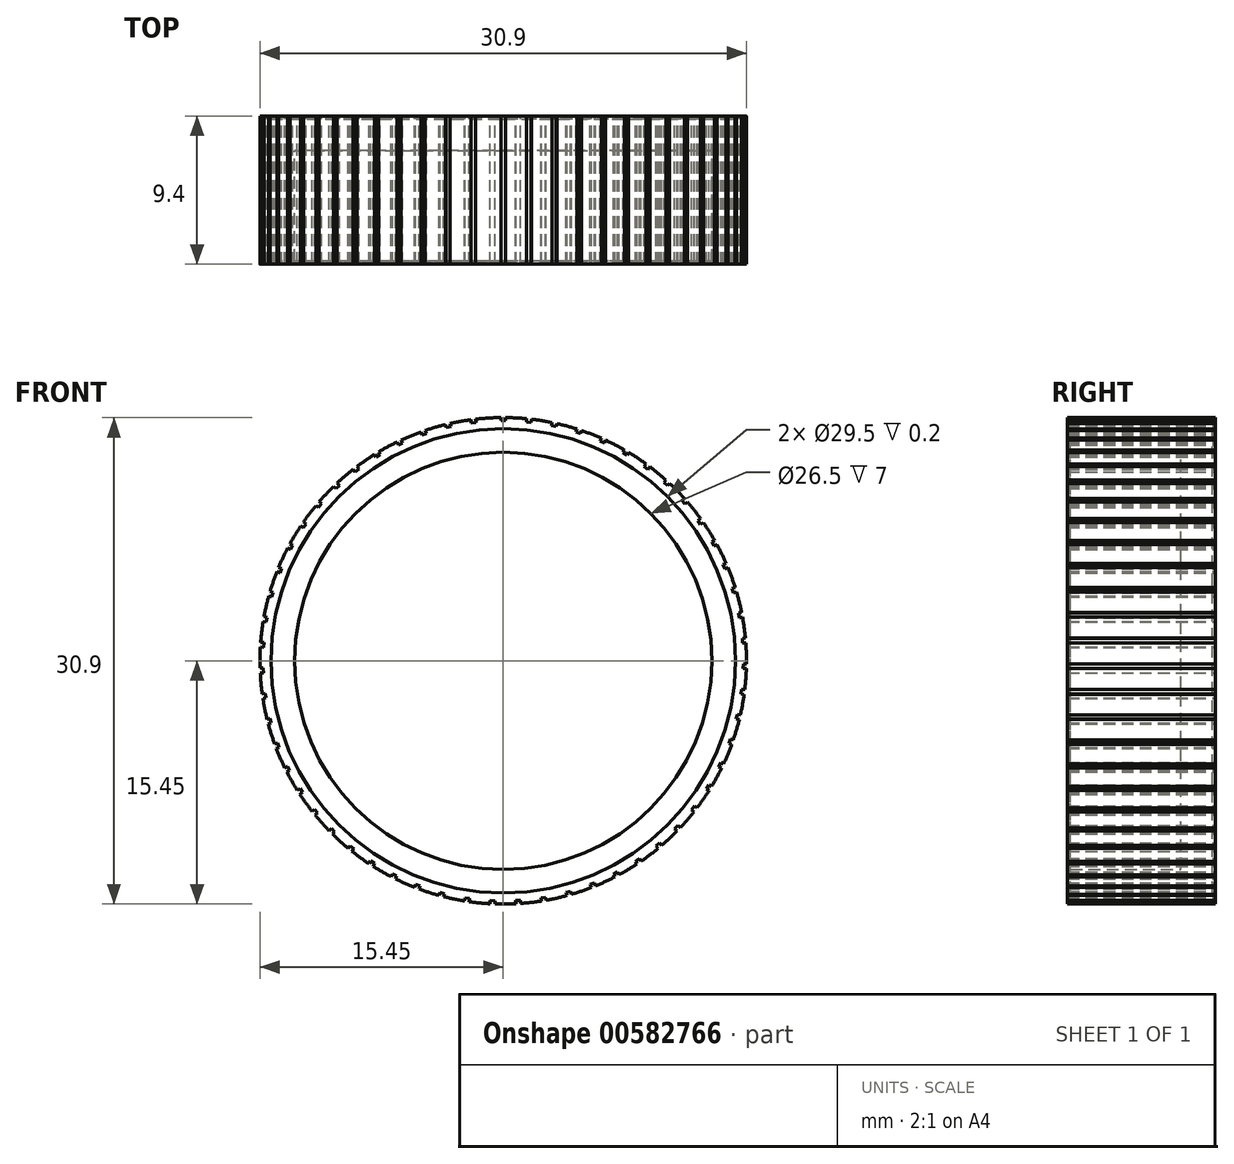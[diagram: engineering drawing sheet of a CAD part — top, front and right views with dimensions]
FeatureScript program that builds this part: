
annotation { "Feature Type Name" : "Feature", "Feature Type Description" : "" }
export const myFeature = defineFeature(function(context is Context, id is Id, definition is map)
    precondition{}
    {
        {
            var Q0;
            Q0=qCreatedBy(makeId("Front.planeOp"),FACE);
            var sketch = newSketch(context, id + "F0", { "sketchPlane" : qUnion([Q0])});
            skCircle(sketch, "E0", {"center": v(0, 0) * mm, "radius": 14.75 * mm});
            skCircle(sketch, "E1.0", {"center": v(0, 0) * mm, "radius": 13.25 * mm});
            skSolve(sketch);
        }
        {
            var Q0;
            Q0=makeQuery(id+"F0.imprint","IMPRINT",FACE,{"disambiguationData":[TD([[makeQuery(id+"F0.imprint","IMPRINT",EDGE,{"derivedFrom":sQuery(id+"F0.wireOp",EDGE,"E0")}),1.0]])]});
            extrude(context, id + "F1", {"entities" : qUnion([Q0]), "depth" : 9 * mm});
        }
        {
            var Q0;
            Q0=qCreatedBy(makeId("Front.planeOp"),FACE);
            var sketch = newSketch(context, id + "F2", { "sketchPlane" : qUnion([Q0])});
            skCircle(sketch, "E2", {"center": v(0, 0) * mm, "radius": 13.25 * mm});
            skSolve(sketch);
        }
        {
            var Q0;
            {var subQ0=sQuery(id+"F2.wireOp",EDGE,"3keaKyCw-Lqcn-IX1E-cnb6-a4ZA5nUTnozF");Q0=makeQuery(id+"F2.imprint","IMPRINT",FACE,{"disambiguationData":[TD([[makeQuery(id+"F2.imprint","IMPRINT",EDGE,{"derivedFrom":subQ0}),1.0]])]});}
            var Q1;
            {var subQ0=sQuery(id+"F2.wireOp",EDGE,"mG6a82be-69iQ-I6sY-IQmd-3RMDi1MG6bG6");Q1=makeQuery(id+"F2.imprint","IMPRINT",FACE,{"disambiguationData":[TD([[makeQuery(id+"F2.imprint","IMPRINT",EDGE,{"derivedFrom":subQ0}),1.0]])]});}
            var Q2;
            {var subQ0=sQuery(id+"F2.wireOp",EDGE,"hU7no7Vv-n9lv-C5YX-Tx9H-Se0t01cKzEbt");Q2=makeQuery(id+"F2.imprint","IMPRINT",FACE,{"disambiguationData":[TD([[makeQuery(id+"F2.imprint","IMPRINT",EDGE,{"derivedFrom":subQ0}),-1.0]])]});}
            var Q3;
            {var subQ0=sQuery(id+"F2.wireOp",EDGE,"w8KxwOBV-seBn-yTGC-fRHL-n6Ncswi49O3E");Q3=makeQuery(id+"F2.imprint","IMPRINT",FACE,{"disambiguationData":[TD([[makeQuery(id+"F2.imprint","IMPRINT",EDGE,{"derivedFrom":subQ0}),1.0]])]});}
            var Q4;
            {var subQ0=sQuery(id+"F2.wireOp",EDGE,"HlxNPSqv-OCNp-PsbN-OUw0-2Dy4POzx889V");Q4=makeQuery(id+"F2.imprint","IMPRINT",FACE,{"disambiguationData":[TD([[makeQuery(id+"F2.imprint","IMPRINT",EDGE,{"derivedFrom":subQ0}),-1.0]])]});}
            var Q5;
            {var subQ0=sQuery(id+"F2.wireOp",EDGE,"GymvrA6v-V9iu-6h20-Pxzl-EcmsKYmL8GNP");Q5=makeQuery(id+"F2.imprint","IMPRINT",FACE,{"disambiguationData":[TD([[makeQuery(id+"F2.imprint","IMPRINT",EDGE,{"derivedFrom":subQ0}),-1.0]])]});}
            var Q6;
            {var subQ0=sQuery(id+"F2.wireOp",EDGE,"8rj0P59o-sSCo-hf25-OtZS-1FKQbejQrVaP");Q6=makeQuery(id+"F2.imprint","IMPRINT",FACE,{"disambiguationData":[TD([[makeQuery(id+"F2.imprint","IMPRINT",EDGE,{"derivedFrom":subQ0}),-1.0]])]});}
            var Q7;
            {var subQ0=sQuery(id+"F2.wireOp",EDGE,"0XGIMpHW-GgJE-la3a-LZoR-t8cl6haSuso4");Q7=makeQuery(id+"F2.imprint","IMPRINT",FACE,{"disambiguationData":[TD([[makeQuery(id+"F2.imprint","IMPRINT",EDGE,{"derivedFrom":subQ0}),-1.0]])]});}
            var Q8;
            {var subQ1=sQuery(id+"F2.wireOp",EDGE,"cdTxKz4M-8jyy-kseZ-T7IN-5LjAP2MmduU8");var subQ11=sQuery(id+"F2.wireOp",EDGE,"QO7leQhL-Iaco-JcvS-EdGk-ymootaYFfpQf");var subQ12=makeQuery(id+"F2.imprint","INTERSECT",VERTEX,{"derivedFrom":[subQ1,subQ11]});Q8=makeQuery(id+"F2.imprint","IMPRINT",FACE,{"disambiguationData":[TD([[makeQuery(id+"F2.imprint","IMPRINT",EDGE,{"disambiguationData":[TD([[subQ12,-1.0]])],"derivedFrom":subQ1}),-1.0]])]});}
            var Q9;
            {var subQ9=sQuery(id+"F2.wireOp",EDGE,"aPjoHP4x-gmIf-1ttG-AxL6-nKyPkYbaChfL");var subQ11=sQuery(id+"F2.wireOp",EDGE,"8Gy7XW5u-FLYC-EZkC-LaJu-Y9E0anSlFcaX");var subQ12=makeQuery(id+"F2.imprint","INTERSECT",VERTEX,{"derivedFrom":[subQ9,subQ11]});Q9=makeQuery(id+"F2.imprint","IMPRINT",FACE,{"disambiguationData":[TD([[makeQuery(id+"F2.imprint","IMPRINT",EDGE,{"disambiguationData":[TD([[subQ12,-1.0]])],"derivedFrom":subQ9}),1.0]])]});}
            var Q10;
            {var subQ3=sQuery(id+"F2.wireOp",EDGE,"oQIrEx9H-TGKM-4inS-EEnm-a9sFU0Elgldt");var subQ10=sQuery(id+"F2.wireOp",EDGE,"GY7wzPKg-8jDN-OJM1-rmuM-SVpCFXL6a0nh");var subQ11=makeQuery(id+"F2.imprint","INTERSECT",VERTEX,{"derivedFrom":[subQ3,subQ10]});Q10=makeQuery(id+"F2.imprint","IMPRINT",FACE,{"disambiguationData":[TD([[makeQuery(id+"F2.imprint","IMPRINT",EDGE,{"disambiguationData":[TD([[subQ11,-1.0]])],"derivedFrom":subQ3}),1.0]])]});}
            var Q11;
            {var subQ7=sQuery(id+"F2.wireOp",EDGE,"PrWXmb39-ACQH-pRjp-kugf-BFPo7j13sEjC");var subQ9=sQuery(id+"F2.wireOp",EDGE,"5D8PRt4u-vBLA-oPdB-r0au-RqC48Tny4yqn");var subQ10=makeQuery(id+"F2.imprint","INTERSECT",VERTEX,{"derivedFrom":[subQ7,subQ9]});Q11=makeQuery(id+"F2.imprint","IMPRINT",FACE,{"disambiguationData":[TD([[makeQuery(id+"F2.imprint","IMPRINT",EDGE,{"disambiguationData":[TD([[subQ10,1.0]])],"derivedFrom":subQ7}),1.0]])]});}
            var Q12;
            {var subQ5=sQuery(id+"F2.wireOp",EDGE,"PrWXmb39-ACQH-pRjp-kugf-BFPo7j13sEjC");var subQ7=sQuery(id+"F2.wireOp",EDGE,"GY7wzPKg-8jDN-OJM1-rmuM-SVpCFXL6a0nh");var subQ12=makeQuery(id+"F2.imprint","INTERSECT",VERTEX,{"derivedFrom":[subQ5,subQ7]});Q12=makeQuery(id+"F2.imprint","IMPRINT",FACE,{"disambiguationData":[TD([[makeQuery(id+"F2.imprint","IMPRINT",EDGE,{"disambiguationData":[TD([[subQ12,-1.0]])],"derivedFrom":subQ5}),-1.0]])]});}
            var Q13;
            {var subQ0=sQuery(id+"F2.wireOp",EDGE,"5D8PRt4u-vBLA-oPdB-r0au-RqC48Tny4yqn");var subQ1=sQuery(id+"F2.wireOp",EDGE,"mz7uVP0I-VIxG-UEDP-77Vf-fuGD4AyohhOF");var subQ2=makeQuery(id+"F2.imprint","INTERSECT",VERTEX,{"derivedFrom":[subQ1,subQ0]});Q13=makeQuery(id+"F2.imprint","IMPRINT",FACE,{"disambiguationData":[TD([[makeQuery(id+"F2.imprint","IMPRINT",EDGE,{"disambiguationData":[TD([[subQ2,1.0]])],"derivedFrom":subQ1}),-1.0]])]});}
            var Q14;
            {var subQ0=sQuery(id+"F2.wireOp",EDGE,"GY7wzPKg-8jDN-OJM1-rmuM-SVpCFXL6a0nh");var subQ8=sQuery(id+"F2.wireOp",EDGE,"eVlDfYWF-ZmK0-dg2n-POrD-hiu8iOGEyNgQ");var subQ14=makeQuery(id+"F2.imprint","INTERSECT",VERTEX,{"derivedFrom":[subQ8,subQ0]});Q14=makeQuery(id+"F2.imprint","IMPRINT",FACE,{"disambiguationData":[TD([[makeQuery(id+"F2.imprint","IMPRINT",EDGE,{"disambiguationData":[TD([[subQ14,1.0]])],"derivedFrom":subQ8}),1.0]])]});}
            var Q15;
            {var subQ0=sQuery(id+"F2.wireOp",EDGE,"8Gy7XW5u-FLYC-EZkC-LaJu-Y9E0anSlFcaX");var subQ1=sQuery(id+"F2.wireOp",EDGE,"pedmM5iB-94l6-CeBW-8z7l-qVik7crMEmoY");var subQ2=makeQuery(id+"F2.imprint","INTERSECT",VERTEX,{"derivedFrom":[subQ1,subQ0]});Q15=makeQuery(id+"F2.imprint","IMPRINT",FACE,{"disambiguationData":[TD([[makeQuery(id+"F2.imprint","IMPRINT",EDGE,{"disambiguationData":[TD([[subQ2,-1.0]])],"derivedFrom":subQ1}),-1.0]])]});}
            var Q16;
            {var subQ3=sQuery(id+"F2.wireOp",EDGE,"aPjoHP4x-gmIf-1ttG-AxL6-nKyPkYbaChfL");var subQ5=sQuery(id+"F2.wireOp",EDGE,"GY7wzPKg-8jDN-OJM1-rmuM-SVpCFXL6a0nh");var subQ10=makeQuery(id+"F2.imprint","INTERSECT",VERTEX,{"derivedFrom":[subQ3,subQ5]});Q16=makeQuery(id+"F2.imprint","IMPRINT",FACE,{"disambiguationData":[TD([[makeQuery(id+"F2.imprint","IMPRINT",EDGE,{"disambiguationData":[TD([[subQ10,1.0]])],"derivedFrom":subQ3}),-1.0]])]});}
            var Q17;
            {var subQ0=sQuery(id+"F2.wireOp",EDGE,"GY7wzPKg-8jDN-OJM1-rmuM-SVpCFXL6a0nh");var subQ1=sQuery(id+"F2.wireOp",EDGE,"eVlDfYWF-ZmK0-dg2n-POrD-hiu8iOGEyNgQ");var subQ2=makeQuery(id+"F2.imprint","INTERSECT",VERTEX,{"derivedFrom":[subQ1,subQ0]});Q17=makeQuery(id+"F2.imprint","IMPRINT",FACE,{"disambiguationData":[TD([[makeQuery(id+"F2.imprint","IMPRINT",EDGE,{"disambiguationData":[TD([[subQ2,1.0]])],"derivedFrom":subQ1}),-1.0]])]});}
            var Q18;
            {var subQ0=sQuery(id+"F2.wireOp",EDGE,"GY7wzPKg-8jDN-OJM1-rmuM-SVpCFXL6a0nh");var subQ1=sQuery(id+"F2.wireOp",EDGE,"nDKB6Nuh-on1I-7DlA-8arG-BoZKlbM7OEjq");var subQ2=makeQuery(id+"F2.imprint","INTERSECT",VERTEX,{"derivedFrom":[subQ1,subQ0]});Q18=makeQuery(id+"F2.imprint","IMPRINT",FACE,{"disambiguationData":[TD([[makeQuery(id+"F2.imprint","IMPRINT",EDGE,{"disambiguationData":[TD([[subQ2,1.0]])],"derivedFrom":subQ1}),1.0]])]});}
            var Q19;
            {var subQ0=sQuery(id+"F2.wireOp",EDGE,"GY7wzPKg-8jDN-OJM1-rmuM-SVpCFXL6a0nh");var subQ1=sQuery(id+"F2.wireOp",EDGE,"pedmM5iB-94l6-CeBW-8z7l-qVik7crMEmoY");var subQ2=makeQuery(id+"F2.imprint","INTERSECT",VERTEX,{"derivedFrom":[subQ1,subQ0]});Q19=makeQuery(id+"F2.imprint","IMPRINT",FACE,{"disambiguationData":[TD([[makeQuery(id+"F2.imprint","IMPRINT",EDGE,{"disambiguationData":[TD([[subQ2,1.0]])],"derivedFrom":subQ1}),-1.0]])]});}
            var Q20;
            {var subQ0=sQuery(id+"F2.wireOp",EDGE,"GY7wzPKg-8jDN-OJM1-rmuM-SVpCFXL6a0nh");var subQ1=sQuery(id+"F2.wireOp",EDGE,"aPjoHP4x-gmIf-1ttG-AxL6-nKyPkYbaChfL");var subQ2=makeQuery(id+"F2.imprint","INTERSECT",VERTEX,{"derivedFrom":[subQ1,subQ0]});Q20=makeQuery(id+"F2.imprint","IMPRINT",FACE,{"disambiguationData":[TD([[makeQuery(id+"F2.imprint","IMPRINT",EDGE,{"disambiguationData":[TD([[subQ2,1.0]])],"derivedFrom":subQ1}),1.0]])]});}
            var Q21;
            {var subQ0=sQuery(id+"F2.wireOp",EDGE,"GY7wzPKg-8jDN-OJM1-rmuM-SVpCFXL6a0nh");var subQ1=sQuery(id+"F2.wireOp",EDGE,"ySy2fclQ-QHqK-LRJv-mab4-BJFxhKYbme3X");var subQ2=makeQuery(id+"F2.imprint","INTERSECT",VERTEX,{"derivedFrom":[subQ1,subQ0]});Q21=makeQuery(id+"F2.imprint","IMPRINT",FACE,{"disambiguationData":[TD([[makeQuery(id+"F2.imprint","IMPRINT",EDGE,{"disambiguationData":[TD([[subQ2,-1.0]])],"derivedFrom":subQ1}),1.0]])]});}
            var Q22;
            {var subQ0=sQuery(id+"F2.wireOp",EDGE,"GY7wzPKg-8jDN-OJM1-rmuM-SVpCFXL6a0nh");var subQ1=sQuery(id+"F2.wireOp",EDGE,"oQIrEx9H-TGKM-4inS-EEnm-a9sFU0Elgldt");var subQ2=makeQuery(id+"F2.imprint","INTERSECT",VERTEX,{"derivedFrom":[subQ1,subQ0]});Q22=makeQuery(id+"F2.imprint","IMPRINT",FACE,{"disambiguationData":[TD([[makeQuery(id+"F2.imprint","IMPRINT",EDGE,{"disambiguationData":[TD([[subQ2,-1.0]])],"derivedFrom":subQ1}),-1.0]])]});}
            var Q23;
            {var subQ0=sQuery(id+"F2.wireOp",EDGE,"GY7wzPKg-8jDN-OJM1-rmuM-SVpCFXL6a0nh");var subQ1=sQuery(id+"F2.wireOp",EDGE,"PrWXmb39-ACQH-pRjp-kugf-BFPo7j13sEjC");var subQ2=makeQuery(id+"F2.imprint","INTERSECT",VERTEX,{"derivedFrom":[subQ1,subQ0]});Q23=makeQuery(id+"F2.imprint","IMPRINT",FACE,{"disambiguationData":[TD([[makeQuery(id+"F2.imprint","IMPRINT",EDGE,{"disambiguationData":[TD([[subQ2,-1.0]])],"derivedFrom":subQ1}),1.0]])]});}
            var Q24;
            {var subQ0=sQuery(id+"F2.wireOp",EDGE,"GY7wzPKg-8jDN-OJM1-rmuM-SVpCFXL6a0nh");var subQ1=sQuery(id+"F2.wireOp",EDGE,"mz7uVP0I-VIxG-UEDP-77Vf-fuGD4AyohhOF");var subQ2=makeQuery(id+"F2.imprint","INTERSECT",VERTEX,{"derivedFrom":[subQ1,subQ0]});Q24=makeQuery(id+"F2.imprint","IMPRINT",FACE,{"disambiguationData":[TD([[makeQuery(id+"F2.imprint","IMPRINT",EDGE,{"disambiguationData":[TD([[subQ2,-1.0]])],"derivedFrom":subQ1}),-1.0]])]});}
            var Q25;
            Q25=makeQuery(id+"F2.imprint","IMPRINT",FACE,{"disambiguationData":[TD([[makeQuery(id+"F2.imprint","IMPRINT",EDGE,{"derivedFrom":sQuery(id+"F2.wireOp",EDGE,"E2")}),1.0]])]});
            extrude(context, id + "F3", {"entities" : qUnion([Q0, Q1, Q2, Q3, Q4, Q5, Q6, Q7, Q8, Q9, Q10, Q11, Q12, Q13, Q14, Q15, Q16, Q17, Q18, Q19, Q20, Q21, Q22, Q23, Q24, Q25]), "operationType" : NewBodyOperationType.ADD, "depth" : 2 * mm});
        }
        {
            var Q0;
            Q0=qCreatedBy(makeId("Front.planeOp"),FACE);
            var sketch = newSketch(context, id + "F4", { "sketchPlane" : qUnion([Q0])});
            skCircle(sketch, "E3", {"center": v(0, 0) * mm, "radius": 15.45 * mm});
            skCircle(sketch, "E4", {"center": v(0, 0) * mm, "radius": 14.75 * mm});
            skLineSegment(sketch, "E5.bottom", {"start": v(0.15, 15.45) * mm, "end": v(-0.15, 15.45) * mm});
            skLineSegment(sketch, "E5.top", {"start": v(0.15, 15.25) * mm, "end": v(-0.15, 15.25) * mm});
            skLineSegment(sketch, "E5.left", {"start": v(0.15, 15.45) * mm, "end": v(0.15, 15.25) * mm});
            skLineSegment(sketch, "E5.right", {"start": v(-0.15, 15.45) * mm, "end": v(-0.15, 15.25) * mm});
            skLineSegment(sketch, "E6.1.0", {"start": v(1.49, 15.38) * mm, "end": v(1.47, 15.18) * mm});
            skLineSegment(sketch, "E6.1.1", {"start": v(1.79, 15.35) * mm, "end": v(1.77, 15.15) * mm});
            skLineSegment(sketch, "E6.1.2", {"start": v(1.77, 15.15) * mm, "end": v(1.47, 15.18) * mm});
            skLineSegment(sketch, "E6.1.3", {"start": v(1.79, 15.35) * mm, "end": v(1.49, 15.38) * mm});
            skLineSegment(sketch, "E6.2.0", {"start": v(3.11, 15.13) * mm, "end": v(3.07, 14.94) * mm});
            skLineSegment(sketch, "E6.2.1", {"start": v(3.4, 15.07) * mm, "end": v(3.36, 14.87) * mm});
            skLineSegment(sketch, "E6.2.2", {"start": v(3.36, 14.87) * mm, "end": v(3.07, 14.94) * mm});
            skLineSegment(sketch, "E6.2.3", {"start": v(3.4, 15.07) * mm, "end": v(3.11, 15.13) * mm});
            skLineSegment(sketch, "E6.3.0", {"start": v(4.7, 14.72) * mm, "end": v(4.63, 14.53) * mm});
            skLineSegment(sketch, "E6.3.1", {"start": v(4.98, 14.62) * mm, "end": v(4.92, 14.43) * mm});
            skLineSegment(sketch, "E6.3.2", {"start": v(4.92, 14.43) * mm, "end": v(4.63, 14.53) * mm});
            skLineSegment(sketch, "E6.3.3", {"start": v(4.98, 14.62) * mm, "end": v(4.7, 14.72) * mm});
            skLineSegment(sketch, "E6.4.0", {"start": v(6.23, 14.14) * mm, "end": v(6.15, 13.96) * mm});
            skLineSegment(sketch, "E6.4.1", {"start": v(6.5, 14.01) * mm, "end": v(6.42, 13.83) * mm});
            skLineSegment(sketch, "E6.4.2", {"start": v(6.42, 13.83) * mm, "end": v(6.15, 13.96) * mm});
            skLineSegment(sketch, "E6.4.3", {"start": v(6.5, 14.01) * mm, "end": v(6.23, 14.14) * mm});
            skLineSegment(sketch, "E6.5.0", {"start": v(7.7, 13.4) * mm, "end": v(7.6, 13.23) * mm});
            skLineSegment(sketch, "E6.5.1", {"start": v(7.95, 13.25) * mm, "end": v(7.85, 13.07) * mm});
            skLineSegment(sketch, "E6.5.2", {"start": v(7.85, 13.07) * mm, "end": v(7.6, 13.23) * mm});
            skLineSegment(sketch, "E6.5.3", {"start": v(7.95, 13.25) * mm, "end": v(7.7, 13.4) * mm});
            skLineSegment(sketch, "E6.6.0", {"start": v(9.07, 12.5) * mm, "end": v(8.95, 12.35) * mm});
            skLineSegment(sketch, "E6.6.1", {"start": v(9.31, 12.33) * mm, "end": v(9.2, 12.17) * mm});
            skLineSegment(sketch, "E6.6.2", {"start": v(9.2, 12.17) * mm, "end": v(8.95, 12.35) * mm});
            skLineSegment(sketch, "E6.6.3", {"start": v(9.31, 12.33) * mm, "end": v(9.07, 12.5) * mm});
            skLineSegment(sketch, "E6.7.0", {"start": v(10.35, 11.47) * mm, "end": v(10.21, 11.33) * mm});
            skLineSegment(sketch, "E6.7.1", {"start": v(10.57, 11.27) * mm, "end": v(10.43, 11.12) * mm});
            skLineSegment(sketch, "E6.7.2", {"start": v(10.43, 11.12) * mm, "end": v(10.21, 11.33) * mm});
            skLineSegment(sketch, "E6.7.3", {"start": v(10.57, 11.27) * mm, "end": v(10.35, 11.47) * mm});
            skLineSegment(sketch, "E6.8.0", {"start": v(11.5, 10.31) * mm, "end": v(11.35, 10.18) * mm});
            skLineSegment(sketch, "E6.8.1", {"start": v(11.7, 10.09) * mm, "end": v(11.55, 9.96) * mm});
            skLineSegment(sketch, "E6.8.2", {"start": v(11.55, 9.96) * mm, "end": v(11.35, 10.18) * mm});
            skLineSegment(sketch, "E6.8.3", {"start": v(11.7, 10.09) * mm, "end": v(11.5, 10.31) * mm});
            skLineSegment(sketch, "E6.9.0", {"start": v(12.53, 9.04) * mm, "end": v(12.37, 8.92) * mm});
            skLineSegment(sketch, "E6.9.1", {"start": v(12.7, 8.8) * mm, "end": v(12.54, 8.68) * mm});
            skLineSegment(sketch, "E6.9.2", {"start": v(12.54, 8.68) * mm, "end": v(12.37, 8.92) * mm});
            skLineSegment(sketch, "E6.9.3", {"start": v(12.7, 8.8) * mm, "end": v(12.53, 9.04) * mm});
            skLineSegment(sketch, "E6.10.0", {"start": v(13.42, 7.66) * mm, "end": v(13.24, 7.56) * mm});
            skLineSegment(sketch, "E6.10.1", {"start": v(13.57, 7.4) * mm, "end": v(13.4, 7.3) * mm});
            skLineSegment(sketch, "E6.10.2", {"start": v(13.4, 7.3) * mm, "end": v(13.24, 7.56) * mm});
            skLineSegment(sketch, "E6.10.3", {"start": v(13.57, 7.4) * mm, "end": v(13.42, 7.66) * mm});
            skLineSegment(sketch, "E6.11.0", {"start": v(14.16, 6.2) * mm, "end": v(13.97, 6.11) * mm});
            skLineSegment(sketch, "E6.11.1", {"start": v(14.27, 5.92) * mm, "end": v(14.09, 5.84) * mm});
            skLineSegment(sketch, "E6.11.2", {"start": v(14.09, 5.84) * mm, "end": v(13.97, 6.11) * mm});
            skLineSegment(sketch, "E6.11.3", {"start": v(14.27, 5.92) * mm, "end": v(14.16, 6.2) * mm});
            skLineSegment(sketch, "E6.12.0", {"start": v(14.73, 4.66) * mm, "end": v(14.54, 4.6) * mm});
            skLineSegment(sketch, "E6.12.1", {"start": v(14.82, 4.37) * mm, "end": v(14.63, 4.31) * mm});
            skLineSegment(sketch, "E6.12.2", {"start": v(14.63, 4.31) * mm, "end": v(14.54, 4.6) * mm});
            skLineSegment(sketch, "E6.12.3", {"start": v(14.82, 4.37) * mm, "end": v(14.73, 4.66) * mm});
            skLineSegment(sketch, "E6.13.0", {"start": v(15.14, 3.07) * mm, "end": v(14.95, 3.03) * mm});
            skLineSegment(sketch, "E6.13.1", {"start": v(15.2, 2.77) * mm, "end": v(15, 2.74) * mm});
            skLineSegment(sketch, "E6.13.2", {"start": v(15, 2.74) * mm, "end": v(14.95, 3.03) * mm});
            skLineSegment(sketch, "E6.13.3", {"start": v(15.2, 2.77) * mm, "end": v(15.14, 3.07) * mm});
            skLineSegment(sketch, "E6.14.0", {"start": v(15.38, 1.45) * mm, "end": v(15.18, 1.43) * mm});
            skLineSegment(sketch, "E6.14.1", {"start": v(15.4, 1.15) * mm, "end": v(15.2, 1.13) * mm});
            skLineSegment(sketch, "E6.14.2", {"start": v(15.2, 1.13) * mm, "end": v(15.18, 1.43) * mm});
            skLineSegment(sketch, "E6.14.3", {"start": v(15.4, 1.15) * mm, "end": v(15.38, 1.45) * mm});
            skLineSegment(sketch, "E6.15.0", {"start": v(15.45, -0.2) * mm, "end": v(15.25, -0.19) * mm});
            skLineSegment(sketch, "E6.15.1", {"start": v(15.44, -0.5) * mm, "end": v(15.24, -0.49) * mm});
            skLineSegment(sketch, "E6.15.2", {"start": v(15.24, -0.49) * mm, "end": v(15.25, -0.19) * mm});
            skLineSegment(sketch, "E6.15.3", {"start": v(15.44, -0.5) * mm, "end": v(15.45, -0.2) * mm});
            skLineSegment(sketch, "E6.16.0", {"start": v(15.34, -1.83) * mm, "end": v(15.14, -1.8) * mm});
            skLineSegment(sketch, "E6.16.1", {"start": v(15.3, -2.13) * mm, "end": v(15.1, -2.1) * mm});
            skLineSegment(sketch, "E6.16.2", {"start": v(15.1, -2.1) * mm, "end": v(15.14, -1.8) * mm});
            skLineSegment(sketch, "E6.16.3", {"start": v(15.3, -2.13) * mm, "end": v(15.34, -1.83) * mm});
            skLineSegment(sketch, "E6.17.0", {"start": v(15.06, -3.45) * mm, "end": v(14.87, -3.4) * mm});
            skLineSegment(sketch, "E6.17.1", {"start": v(15, -3.74) * mm, "end": v(14.8, -3.7) * mm});
            skLineSegment(sketch, "E6.17.2", {"start": v(14.8, -3.7) * mm, "end": v(14.87, -3.4) * mm});
            skLineSegment(sketch, "E6.17.3", {"start": v(15, -3.74) * mm, "end": v(15.06, -3.45) * mm});
            skLineSegment(sketch, "E6.18.0", {"start": v(14.61, -5.02) * mm, "end": v(14.42, -4.96) * mm});
            skLineSegment(sketch, "E6.18.1", {"start": v(14.51, -5.3) * mm, "end": v(14.32, -5.24) * mm});
            skLineSegment(sketch, "E6.18.2", {"start": v(14.32, -5.24) * mm, "end": v(14.42, -4.96) * mm});
            skLineSegment(sketch, "E6.18.3", {"start": v(14.51, -5.3) * mm, "end": v(14.61, -5.02) * mm});
            skLineSegment(sketch, "E6.19.0", {"start": v(14, -6.54) * mm, "end": v(13.82, -6.46) * mm});
            skLineSegment(sketch, "E6.19.1", {"start": v(13.87, -6.81) * mm, "end": v(13.69, -6.73) * mm});
            skLineSegment(sketch, "E6.19.2", {"start": v(13.69, -6.73) * mm, "end": v(13.82, -6.46) * mm});
            skLineSegment(sketch, "E6.19.3", {"start": v(13.87, -6.81) * mm, "end": v(14, -6.54) * mm});
            skLineSegment(sketch, "E6.20.0", {"start": v(13.22, -7.99) * mm, "end": v(13.05, -7.88) * mm});
            skLineSegment(sketch, "E6.20.1", {"start": v(13.07, -8.24) * mm, "end": v(12.9, -8.14) * mm});
            skLineSegment(sketch, "E6.20.2", {"start": v(12.9, -8.14) * mm, "end": v(13.05, -7.88) * mm});
            skLineSegment(sketch, "E6.20.3", {"start": v(13.07, -8.24) * mm, "end": v(13.22, -7.99) * mm});
            skLineSegment(sketch, "E6.21.0", {"start": v(12.3, -9.35) * mm, "end": v(12.14, -9.22) * mm});
            skLineSegment(sketch, "E6.21.1", {"start": v(12.12, -9.58) * mm, "end": v(11.96, -9.46) * mm});
            skLineSegment(sketch, "E6.21.2", {"start": v(11.96, -9.46) * mm, "end": v(12.14, -9.22) * mm});
            skLineSegment(sketch, "E6.21.3", {"start": v(12.12, -9.58) * mm, "end": v(12.3, -9.35) * mm});
            skLineSegment(sketch, "E6.22.0", {"start": v(11.24, -10.6) * mm, "end": v(11.1, -10.46) * mm});
            skLineSegment(sketch, "E6.22.1", {"start": v(11.03, -10.81) * mm, "end": v(10.9, -10.68) * mm});
            skLineSegment(sketch, "E6.22.2", {"start": v(10.9, -10.68) * mm, "end": v(11.1, -10.46) * mm});
            skLineSegment(sketch, "E6.22.3", {"start": v(11.03, -10.81) * mm, "end": v(11.24, -10.6) * mm});
            skLineSegment(sketch, "E6.23.0", {"start": v(10.06, -11.73) * mm, "end": v(9.93, -11.58) * mm});
            skLineSegment(sketch, "E6.23.1", {"start": v(9.83, -11.92) * mm, "end": v(9.7, -11.77) * mm});
            skLineSegment(sketch, "E6.23.2", {"start": v(9.7, -11.77) * mm, "end": v(9.93, -11.58) * mm});
            skLineSegment(sketch, "E6.23.3", {"start": v(9.83, -11.92) * mm, "end": v(10.06, -11.73) * mm});
            skLineSegment(sketch, "E6.24.0", {"start": v(8.76, -12.73) * mm, "end": v(8.64, -12.56) * mm});
            skLineSegment(sketch, "E6.24.1", {"start": v(8.5, -12.9) * mm, "end": v(8.4, -12.73) * mm});
            skLineSegment(sketch, "E6.24.2", {"start": v(8.4, -12.73) * mm, "end": v(8.64, -12.56) * mm});
            skLineSegment(sketch, "E6.24.3", {"start": v(8.5, -12.9) * mm, "end": v(8.76, -12.73) * mm});
            skLineSegment(sketch, "E6.25.0", {"start": v(7.36, -13.59) * mm, "end": v(7.26, -13.4) * mm});
            skLineSegment(sketch, "E6.25.1", {"start": v(7.1, -13.73) * mm, "end": v(7, -13.55) * mm});
            skLineSegment(sketch, "E6.25.2", {"start": v(7, -13.55) * mm, "end": v(7.26, -13.4) * mm});
            skLineSegment(sketch, "E6.25.3", {"start": v(7.1, -13.73) * mm, "end": v(7.36, -13.59) * mm});
            skLineSegment(sketch, "E6.26.0", {"start": v(5.88, -14.29) * mm, "end": v(5.8, -14.1) * mm});
            skLineSegment(sketch, "E6.26.1", {"start": v(5.6, -14.4) * mm, "end": v(5.52, -14.21) * mm});
            skLineSegment(sketch, "E6.26.2", {"start": v(5.52, -14.21) * mm, "end": v(5.8, -14.1) * mm});
            skLineSegment(sketch, "E6.26.3", {"start": v(5.6, -14.4) * mm, "end": v(5.88, -14.29) * mm});
            skLineSegment(sketch, "E6.27.0", {"start": v(4.33, -14.83) * mm, "end": v(4.27, -14.64) * mm});
            skLineSegment(sketch, "E6.27.1", {"start": v(4.04, -14.91) * mm, "end": v(3.99, -14.72) * mm});
            skLineSegment(sketch, "E6.27.2", {"start": v(3.99, -14.72) * mm, "end": v(4.27, -14.64) * mm});
            skLineSegment(sketch, "E6.27.3", {"start": v(4.04, -14.91) * mm, "end": v(4.33, -14.83) * mm});
            skLineSegment(sketch, "E6.28.0", {"start": v(2.73, -15.2) * mm, "end": v(2.7, -15) * mm});
            skLineSegment(sketch, "E6.28.1", {"start": v(2.44, -15.26) * mm, "end": v(2.4, -15.06) * mm});
            skLineSegment(sketch, "E6.28.2", {"start": v(2.4, -15.06) * mm, "end": v(2.7, -15) * mm});
            skLineSegment(sketch, "E6.28.3", {"start": v(2.44, -15.26) * mm, "end": v(2.73, -15.2) * mm});
            skLineSegment(sketch, "E6.29.0", {"start": v(1.1, -15.41) * mm, "end": v(1.1, -15.21) * mm});
            skLineSegment(sketch, "E6.29.1", {"start": v(0.8, -15.43) * mm, "end": v(0.8, -15.23) * mm});
            skLineSegment(sketch, "E6.29.2", {"start": v(0.8, -15.23) * mm, "end": v(1.1, -15.21) * mm});
            skLineSegment(sketch, "E6.29.3", {"start": v(0.8, -15.43) * mm, "end": v(1.1, -15.41) * mm});
            skLineSegment(sketch, "E6.30.0", {"start": v(-0.54, -15.44) * mm, "end": v(-0.53, -15.24) * mm});
            skLineSegment(sketch, "E6.30.1", {"start": v(-0.84, -15.43) * mm, "end": v(-0.83, -15.23) * mm});
            skLineSegment(sketch, "E6.30.2", {"start": v(-0.83, -15.23) * mm, "end": v(-0.53, -15.24) * mm});
            skLineSegment(sketch, "E6.30.3", {"start": v(-0.84, -15.43) * mm, "end": v(-0.54, -15.44) * mm});
            skLineSegment(sketch, "E6.31.0", {"start": v(-2.17, -15.3) * mm, "end": v(-2.14, -15.1) * mm});
            skLineSegment(sketch, "E6.31.1", {"start": v(-2.47, -15.25) * mm, "end": v(-2.44, -15.05) * mm});
            skLineSegment(sketch, "E6.31.2", {"start": v(-2.44, -15.05) * mm, "end": v(-2.14, -15.1) * mm});
            skLineSegment(sketch, "E6.31.3", {"start": v(-2.47, -15.25) * mm, "end": v(-2.17, -15.3) * mm});
            skLineSegment(sketch, "E6.32.0", {"start": v(-3.78, -14.98) * mm, "end": v(-3.73, -14.79) * mm});
            skLineSegment(sketch, "E6.32.1", {"start": v(-4.07, -14.9) * mm, "end": v(-4.02, -14.71) * mm});
            skLineSegment(sketch, "E6.32.2", {"start": v(-4.02, -14.71) * mm, "end": v(-3.73, -14.79) * mm});
            skLineSegment(sketch, "E6.32.3", {"start": v(-4.07, -14.9) * mm, "end": v(-3.78, -14.98) * mm});
            skLineSegment(sketch, "E6.33.0", {"start": v(-5.35, -14.5) * mm, "end": v(-5.27, -14.3) * mm});
            skLineSegment(sketch, "E6.33.1", {"start": v(-5.63, -14.39) * mm, "end": v(-5.55, -14.2) * mm});
            skLineSegment(sketch, "E6.33.2", {"start": v(-5.55, -14.2) * mm, "end": v(-5.27, -14.3) * mm});
            skLineSegment(sketch, "E6.33.3", {"start": v(-5.63, -14.39) * mm, "end": v(-5.35, -14.5) * mm});
            skLineSegment(sketch, "E6.34.0", {"start": v(-6.85, -13.85) * mm, "end": v(-6.76, -13.67) * mm});
            skLineSegment(sketch, "E6.34.1", {"start": v(-7.12, -13.71) * mm, "end": v(-7.03, -13.53) * mm});
            skLineSegment(sketch, "E6.34.2", {"start": v(-7.03, -13.53) * mm, "end": v(-6.76, -13.67) * mm});
            skLineSegment(sketch, "E6.34.3", {"start": v(-7.12, -13.71) * mm, "end": v(-6.85, -13.85) * mm});
            skLineSegment(sketch, "E6.35.0", {"start": v(-8.28, -13.04) * mm, "end": v(-8.17, -12.88) * mm});
            skLineSegment(sketch, "E6.35.1", {"start": v(-8.53, -12.88) * mm, "end": v(-8.42, -12.71) * mm});
            skLineSegment(sketch, "E6.35.2", {"start": v(-8.42, -12.71) * mm, "end": v(-8.17, -12.88) * mm});
            skLineSegment(sketch, "E6.35.3", {"start": v(-8.53, -12.88) * mm, "end": v(-8.28, -13.04) * mm});
            skLineSegment(sketch, "E6.36.0", {"start": v(-9.62, -12.1) * mm, "end": v(-9.5, -11.94) * mm});
            skLineSegment(sketch, "E6.36.1", {"start": v(-9.85, -11.9) * mm, "end": v(-9.72, -11.75) * mm});
            skLineSegment(sketch, "E6.36.2", {"start": v(-9.72, -11.75) * mm, "end": v(-9.5, -11.94) * mm});
            skLineSegment(sketch, "E6.36.3", {"start": v(-9.85, -11.9) * mm, "end": v(-9.62, -12.1) * mm});
            skLineSegment(sketch, "E6.37.0", {"start": v(-10.84, -11) * mm, "end": v(-10.7, -10.86) * mm});
            skLineSegment(sketch, "E6.37.1", {"start": v(-11.06, -10.8) * mm, "end": v(-10.91, -10.65) * mm});
            skLineSegment(sketch, "E6.37.2", {"start": v(-10.91, -10.65) * mm, "end": v(-10.7, -10.86) * mm});
            skLineSegment(sketch, "E6.37.3", {"start": v(-11.06, -10.8) * mm, "end": v(-10.84, -11) * mm});
            skLineSegment(sketch, "E6.38.0", {"start": v(-11.95, -9.8) * mm, "end": v(-11.8, -9.67) * mm});
            skLineSegment(sketch, "E6.38.1", {"start": v(-12.14, -9.56) * mm, "end": v(-11.98, -9.43) * mm});
            skLineSegment(sketch, "E6.38.2", {"start": v(-11.98, -9.43) * mm, "end": v(-11.8, -9.67) * mm});
            skLineSegment(sketch, "E6.38.3", {"start": v(-12.14, -9.56) * mm, "end": v(-11.95, -9.8) * mm});
            skLineSegment(sketch, "E6.39.0", {"start": v(-12.92, -8.47) * mm, "end": v(-12.75, -8.36) * mm});
            skLineSegment(sketch, "E6.39.1", {"start": v(-13.08, -8.22) * mm, "end": v(-12.91, -8.11) * mm});
            skLineSegment(sketch, "E6.39.2", {"start": v(-12.91, -8.11) * mm, "end": v(-12.75, -8.36) * mm});
            skLineSegment(sketch, "E6.39.3", {"start": v(-13.08, -8.22) * mm, "end": v(-12.92, -8.47) * mm});
            skLineSegment(sketch, "E6.40.0", {"start": v(-13.75, -7.05) * mm, "end": v(-13.57, -6.96) * mm});
            skLineSegment(sketch, "E6.40.1", {"start": v(-13.88, -6.79) * mm, "end": v(-13.7, -6.7) * mm});
            skLineSegment(sketch, "E6.40.2", {"start": v(-13.7, -6.7) * mm, "end": v(-13.57, -6.96) * mm});
            skLineSegment(sketch, "E6.40.3", {"start": v(-13.88, -6.79) * mm, "end": v(-13.75, -7.05) * mm});
            skLineSegment(sketch, "E6.41.0", {"start": v(-14.42, -5.56) * mm, "end": v(-14.23, -5.49) * mm});
            skLineSegment(sketch, "E6.41.1", {"start": v(-14.52, -5.28) * mm, "end": v(-14.33, -5.2) * mm});
            skLineSegment(sketch, "E6.41.2", {"start": v(-14.33, -5.2) * mm, "end": v(-14.23, -5.49) * mm});
            skLineSegment(sketch, "E6.41.3", {"start": v(-14.52, -5.28) * mm, "end": v(-14.42, -5.56) * mm});
            skLineSegment(sketch, "E6.42.0", {"start": v(-14.92, -4) * mm, "end": v(-14.73, -3.95) * mm});
            skLineSegment(sketch, "E6.42.1", {"start": v(-15, -3.7) * mm, "end": v(-14.8, -3.66) * mm});
            skLineSegment(sketch, "E6.42.2", {"start": v(-14.8, -3.66) * mm, "end": v(-14.73, -3.95) * mm});
            skLineSegment(sketch, "E6.42.3", {"start": v(-15, -3.7) * mm, "end": v(-14.92, -4) * mm});
            skLineSegment(sketch, "E6.43.0", {"start": v(-15.26, -2.4) * mm, "end": v(-15.07, -2.36) * mm});
            skLineSegment(sketch, "E6.43.1", {"start": v(-15.3, -2.1) * mm, "end": v(-15.1, -2.07) * mm});
            skLineSegment(sketch, "E6.43.2", {"start": v(-15.1, -2.07) * mm, "end": v(-15.07, -2.36) * mm});
            skLineSegment(sketch, "E6.43.3", {"start": v(-15.3, -2.1) * mm, "end": v(-15.26, -2.4) * mm});
            skLineSegment(sketch, "E6.44.0", {"start": v(-15.43, -0.76) * mm, "end": v(-15.23, -0.75) * mm});
            skLineSegment(sketch, "E6.44.1", {"start": v(-15.44, -0.46) * mm, "end": v(-15.24, -0.45) * mm});
            skLineSegment(sketch, "E6.44.2", {"start": v(-15.24, -0.45) * mm, "end": v(-15.23, -0.75) * mm});
            skLineSegment(sketch, "E6.44.3", {"start": v(-15.44, -0.46) * mm, "end": v(-15.43, -0.76) * mm});
            skLineSegment(sketch, "E6.45.0", {"start": v(-15.43, 0.88) * mm, "end": v(-15.23, 0.86) * mm});
            skLineSegment(sketch, "E6.45.1", {"start": v(-15.4, 1.18) * mm, "end": v(-15.2, 1.16) * mm});
            skLineSegment(sketch, "E6.45.2", {"start": v(-15.2, 1.16) * mm, "end": v(-15.23, 0.86) * mm});
            skLineSegment(sketch, "E6.45.3", {"start": v(-15.4, 1.18) * mm, "end": v(-15.43, 0.88) * mm});
            skLineSegment(sketch, "E6.46.0", {"start": v(-15.25, 2.5) * mm, "end": v(-15.05, 2.47) * mm});
            skLineSegment(sketch, "E6.46.1", {"start": v(-15.2, 2.8) * mm, "end": v(-15, 2.77) * mm});
            skLineSegment(sketch, "E6.46.2", {"start": v(-15, 2.77) * mm, "end": v(-15.05, 2.47) * mm});
            skLineSegment(sketch, "E6.46.3", {"start": v(-15.2, 2.8) * mm, "end": v(-15.25, 2.5) * mm});
            skLineSegment(sketch, "E6.47.0", {"start": v(-14.9, 4.1) * mm, "end": v(-14.7, 4.05) * mm});
            skLineSegment(sketch, "E6.47.1", {"start": v(-14.81, 4.4) * mm, "end": v(-14.62, 4.34) * mm});
            skLineSegment(sketch, "E6.47.2", {"start": v(-14.62, 4.34) * mm, "end": v(-14.7, 4.05) * mm});
            skLineSegment(sketch, "E6.47.3", {"start": v(-14.81, 4.4) * mm, "end": v(-14.9, 4.1) * mm});
            skLineSegment(sketch, "E6.48.0", {"start": v(-14.37, 5.67) * mm, "end": v(-14.19, 5.6) * mm});
            skLineSegment(sketch, "E6.48.1", {"start": v(-14.26, 5.94) * mm, "end": v(-14.08, 5.87) * mm});
            skLineSegment(sketch, "E6.48.2", {"start": v(-14.08, 5.87) * mm, "end": v(-14.19, 5.6) * mm});
            skLineSegment(sketch, "E6.48.3", {"start": v(-14.26, 5.94) * mm, "end": v(-14.37, 5.67) * mm});
            skLineSegment(sketch, "E6.49.0", {"start": v(-13.7, 7.16) * mm, "end": v(-13.52, 7.06) * mm});
            skLineSegment(sketch, "E6.49.1", {"start": v(-13.55, 7.42) * mm, "end": v(-13.37, 7.33) * mm});
            skLineSegment(sketch, "E6.49.2", {"start": v(-13.37, 7.33) * mm, "end": v(-13.52, 7.06) * mm});
            skLineSegment(sketch, "E6.49.3", {"start": v(-13.55, 7.42) * mm, "end": v(-13.7, 7.16) * mm});
            skLineSegment(sketch, "E6.50.0", {"start": v(-12.86, 8.57) * mm, "end": v(-12.7, 8.46) * mm});
            skLineSegment(sketch, "E6.50.1", {"start": v(-12.69, 8.82) * mm, "end": v(-12.52, 8.7) * mm});
            skLineSegment(sketch, "E6.50.2", {"start": v(-12.52, 8.7) * mm, "end": v(-12.7, 8.46) * mm});
            skLineSegment(sketch, "E6.50.3", {"start": v(-12.69, 8.82) * mm, "end": v(-12.86, 8.57) * mm});
            skLineSegment(sketch, "E6.51.0", {"start": v(-11.88, 9.88) * mm, "end": v(-11.72, 9.75) * mm});
            skLineSegment(sketch, "E6.51.1", {"start": v(-11.68, 10.11) * mm, "end": v(-11.53, 9.98) * mm});
            skLineSegment(sketch, "E6.51.2", {"start": v(-11.53, 9.98) * mm, "end": v(-11.72, 9.75) * mm});
            skLineSegment(sketch, "E6.51.3", {"start": v(-11.68, 10.11) * mm, "end": v(-11.88, 9.88) * mm});
            skLineSegment(sketch, "E6.52.0", {"start": v(-10.76, 11.09) * mm, "end": v(-10.62, 10.94) * mm});
            skLineSegment(sketch, "E6.52.1", {"start": v(-10.54, 11.3) * mm, "end": v(-10.4, 11.15) * mm});
            skLineSegment(sketch, "E6.52.2", {"start": v(-10.4, 11.15) * mm, "end": v(-10.62, 10.94) * mm});
            skLineSegment(sketch, "E6.52.3", {"start": v(-10.54, 11.3) * mm, "end": v(-10.76, 11.09) * mm});
            skLineSegment(sketch, "E6.53.0", {"start": v(-9.53, 12.16) * mm, "end": v(-9.4, 12) * mm});
            skLineSegment(sketch, "E6.53.1", {"start": v(-9.29, 12.35) * mm, "end": v(-9.17, 12.19) * mm});
            skLineSegment(sketch, "E6.53.2", {"start": v(-9.17, 12.19) * mm, "end": v(-9.4, 12) * mm});
            skLineSegment(sketch, "E6.53.3", {"start": v(-9.29, 12.35) * mm, "end": v(-9.53, 12.16) * mm});
            skLineSegment(sketch, "E6.54.0", {"start": v(-8.18, 13.1) * mm, "end": v(-8.08, 12.93) * mm});
            skLineSegment(sketch, "E6.54.1", {"start": v(-7.93, 13.26) * mm, "end": v(-7.82, 13.1) * mm});
            skLineSegment(sketch, "E6.54.2", {"start": v(-7.82, 13.1) * mm, "end": v(-8.08, 12.93) * mm});
            skLineSegment(sketch, "E6.54.3", {"start": v(-7.93, 13.26) * mm, "end": v(-8.18, 13.1) * mm});
            skLineSegment(sketch, "E6.55.0", {"start": v(-6.75, 13.9) * mm, "end": v(-6.66, 13.72) * mm});
            skLineSegment(sketch, "E6.55.1", {"start": v(-6.48, 14.03) * mm, "end": v(-6.4, 13.85) * mm});
            skLineSegment(sketch, "E6.55.2", {"start": v(-6.4, 13.85) * mm, "end": v(-6.66, 13.72) * mm});
            skLineSegment(sketch, "E6.55.3", {"start": v(-6.48, 14.03) * mm, "end": v(-6.75, 13.9) * mm});
            skLineSegment(sketch, "E6.56.0", {"start": v(-5.24, 14.54) * mm, "end": v(-5.17, 14.35) * mm});
            skLineSegment(sketch, "E6.56.1", {"start": v(-4.95, 14.63) * mm, "end": v(-4.89, 14.45) * mm});
            skLineSegment(sketch, "E6.56.2", {"start": v(-4.89, 14.45) * mm, "end": v(-5.17, 14.35) * mm});
            skLineSegment(sketch, "E6.56.3", {"start": v(-4.95, 14.63) * mm, "end": v(-5.24, 14.54) * mm});
            skLineSegment(sketch, "E6.57.0", {"start": v(-3.67, 15) * mm, "end": v(-3.62, 14.81) * mm});
            skLineSegment(sketch, "E6.57.1", {"start": v(-3.37, 15.08) * mm, "end": v(-3.33, 14.88) * mm});
            skLineSegment(sketch, "E6.57.2", {"start": v(-3.33, 14.88) * mm, "end": v(-3.62, 14.81) * mm});
            skLineSegment(sketch, "E6.57.3", {"start": v(-3.37, 15.08) * mm, "end": v(-3.67, 15) * mm});
            skLineSegment(sketch, "E6.58.0", {"start": v(-2.05, 15.31) * mm, "end": v(-2.03, 15.11) * mm});
            skLineSegment(sketch, "E6.58.1", {"start": v(-1.76, 15.35) * mm, "end": v(-1.73, 15.15) * mm});
            skLineSegment(sketch, "E6.58.2", {"start": v(-1.73, 15.15) * mm, "end": v(-2.03, 15.11) * mm});
            skLineSegment(sketch, "E6.58.3", {"start": v(-1.76, 15.35) * mm, "end": v(-2.05, 15.31) * mm});
            skLineSegment(sketch, "E6.59.0", {"start": v(-0.42, 15.44) * mm, "end": v(-0.42, 15.24) * mm});
            skLineSegment(sketch, "E6.59.1", {"start": v(-0.12, 15.45) * mm, "end": v(-0.12, 15.25) * mm});
            skLineSegment(sketch, "E6.59.2", {"start": v(-0.12, 15.25) * mm, "end": v(-0.42, 15.24) * mm});
            skLineSegment(sketch, "E6.59.3", {"start": v(-0.12, 15.45) * mm, "end": v(-0.42, 15.44) * mm});
            skLineSegment(sketch, "E6.anchor1", {"start": v(0, 0) * mm, "end": v(-0.15, 15.25) * mm, "construction": true});
            skLineSegment(sketch, "E6.anchor2", {"start": v(0, 0) * mm, "end": v(-0.42, 15.24) * mm, "construction": true});
            skSolve(sketch);
        }
        {
            var Q0;
            Q0=makeQuery(id+"F4.imprint","IMPRINT",FACE,{"disambiguationData":[TD([[makeQuery(id+"F4.imprint","IMPRINT",EDGE,{"derivedFrom":sQuery(id+"F4.wireOp",EDGE,"E4")}),-1.0]])]});
            var Q1;
            {var subQ1=sQuery(id+"F4.wireOp",EDGE,"E6.59.0");Q1=makeQuery(id+"F4.imprint","IMPRINT",FACE,{"disambiguationData":[TD([[makeQuery(id+"F4.imprint","IMPRINT",EDGE,{"derivedFrom":subQ1}),1.0]])]});}
            extrude(context, id + "F5", {"entities" : qUnion([Q0, Q1]), "operationType" : NewBodyOperationType.ADD, "depth" : 9.2 * mm});
        }
        {
            var Q0;
            Q0=makeQuery(id+"F4.imprint","IMPRINT",FACE,{"disambiguationData":[TD([[makeQuery(id+"F4.imprint","IMPRINT",EDGE,{"derivedFrom":sQuery(id+"F4.wireOp",EDGE,"E4")}),-1.0]])]});
            var Q1;
            {var subQ1=sQuery(id+"F4.wireOp",EDGE,"E6.59.0");Q1=makeQuery(id+"F4.imprint","IMPRINT",FACE,{"disambiguationData":[TD([[makeQuery(id+"F4.imprint","IMPRINT",EDGE,{"derivedFrom":subQ1}),1.0]])]});}
            extrude(context, id + "F6", {"entities" : qUnion([Q0, Q1]), "operationType" : NewBodyOperationType.ADD, "oppositeDirection" : true, "depth" : 0.2 * mm});
        }
    });
